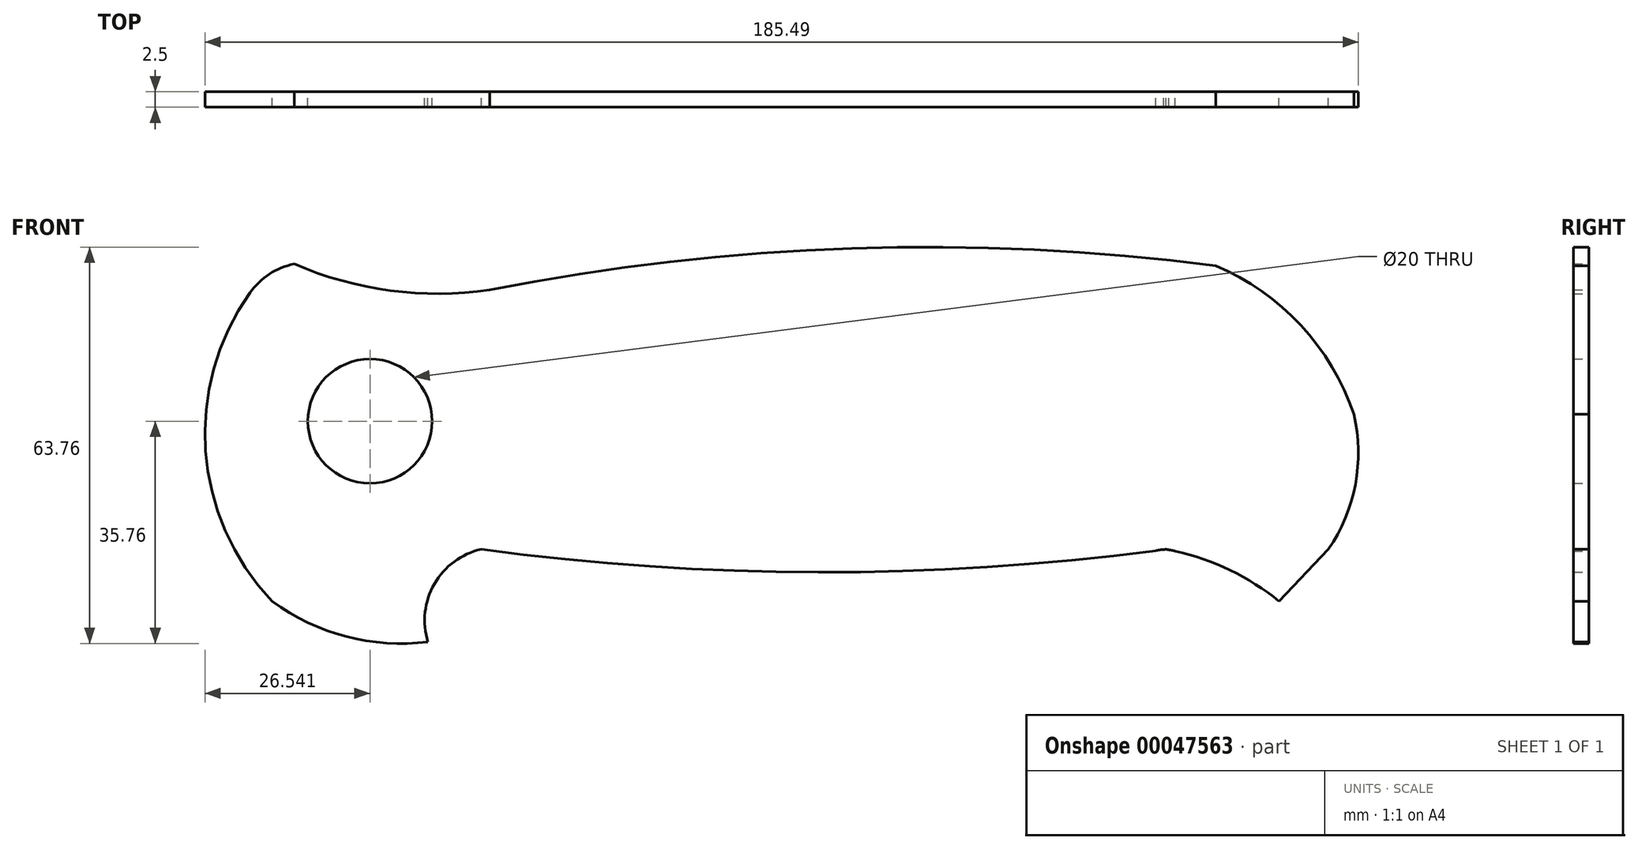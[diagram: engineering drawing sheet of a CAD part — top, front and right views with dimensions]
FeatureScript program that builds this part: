
annotation { "Feature Type Name" : "Feature", "Feature Type Description" : "" }
export const myFeature = defineFeature(function(context is Context, id is Id, definition is map)
    precondition{}
    {
        {
            var Q0;
            Q0=qCreatedBy(makeId("Front.planeOp"),FACE);
            var sketch = newSketch(context, id + "F0", { "sketchPlane" : qUnion([Q0])});
            skPoint(sketch, "E0.start.orphan", {"position": v(13.34, 2.67) * mm});
            skPoint(sketch, "E1.end.orphan", {"position": v(-22.24, -2.7) * mm});
            skPoint(sketch, "E1.start.orphan", {"position": v(-22.24, 18.65) * mm});
            skPoint(sketch, "E2.end.orphan", {"position": v(98.64, 2.67) * mm});
            skPoint(sketch, "E3.start.orphan", {"position": v(151.74, 0) * mm});
            skLineSegment(sketch, "E4.bottom", {"start": v(2.38, 0) * mm, "end": v(4.2, 0) * mm});
            skArc(sketch, "E5", {"start": v(173.95, -23.89) * mm, "mid": v(165.41, -9.56) * mm, "end": v(151.74, 0) * mm});
            skArc(sketch, "E6", {"start": v(169.86, -45.6) * mm, "mid": v(174.19, -35.18) * mm, "end": v(173.95, -23.89) * mm});
            skLineSegment(sketch, "E7", {"start": v(169.86, -45.6) * mm, "end": v(161.9, -53.97) * mm});
            skArc(sketch, "E8", {"start": v(161.9, -53.97) * mm, "mid": v(153.35, -48.62) * mm, "end": v(143.72, -45.6) * mm});
            skArc(sketch, "E9", {"start": v(33.6, -45.6) * mm, "mid": v(88.66, -49.3) * mm, "end": v(143.72, -45.6) * mm});
            skArc(sketch, "E10", {"start": v(145.2, -45.9) * mm, "mid": v(143.63, -45.65) * mm, "end": v(142.05, -45.83) * mm});
            skArc(sketch, "E11", {"start": v(-3.5, -4.21) * mm, "mid": v(-10.73, -29.72) * mm, "end": v(0, -53.97) * mm});
            skArc(sketch, "E12", {"start": v(0, -53.97) * mm, "mid": v(11.88, -59.64) * mm, "end": v(25.02, -60.49) * mm});
            skArc(sketch, "E13", {"start": v(33.6, -45.6) * mm, "mid": v(26.06, -51.17) * mm, "end": v(25.02, -60.49) * mm});
            skCircle(sketch, "E14", {"center": v(15.71, -25) * mm, "radius": 10 * mm});
            skArc(sketch, "E15", {"start": v(3.52, 0.29) * mm, "mid": v(-0.46, -1.33) * mm, "end": v(-3.57, -4.3) * mm});
            skArc(sketch, "E16", {"start": v(3.52, 0.29) * mm, "mid": v(18.96, -3.98) * mm, "end": v(34.97, -3.9) * mm});
            skArc(sketch, "E17", {"start": v(151.74, 0) * mm, "mid": v(93.2, 2.8) * mm, "end": v(34.97, -3.9) * mm});
            skSolve(sketch);
        }
        {
            var Q0;
            {var subQ0=sQuery(id+"F0.wireOp",EDGE,"E15");var subQ3=sQuery(id+"F0.wireOp",EDGE,"E4.bottom");var subQ4=makeQuery(id+"F0.imprint","INTERSECT",VERTEX,{"derivedFrom":[subQ3,subQ0]});Q0=makeQuery(id+"F0.imprint","IMPRINT",FACE,{"disambiguationData":[TD([[makeQuery(id+"F0.imprint","IMPRINT",EDGE,{"disambiguationData":[TD([[subQ4,-1.0]])],"derivedFrom":subQ3}),1.0]])]});}
            var Q1;
            {var subQ0=sQuery(id+"F0.wireOp",EDGE,"E17");var subQ1=sQuery(id+"F0.wireOp",EDGE,"E4.bottom");var subQ2=makeQuery(id+"F0.imprint","INTERSECT",VERTEX,{"derivedFrom":[subQ1,subQ0]});Q1=makeQuery(id+"F0.imprint","IMPRINT",FACE,{"disambiguationData":[TD([[makeQuery(id+"F0.imprint","IMPRINT",EDGE,{"disambiguationData":[TD([[subQ2,-1.0]])],"derivedFrom":subQ1}),1.0]])]});}
            var Q2;
            {var subQ0=sQuery(id+"F0.wireOp",EDGE,"E12");Q2=makeQuery(id+"F0.imprint","IMPRINT",FACE,{"disambiguationData":[TD([[makeQuery(id+"F0.imprint","IMPRINT",EDGE,{"derivedFrom":subQ0}),1.0]])]});}
            var Q3;
            {var subQ2=sQuery(id+"F0.wireOp",EDGE,"E4.right");Q3=makeQuery(id+"F0.imprint","IMPRINT",FACE,{"disambiguationData":[TD([[makeQuery(id+"F0.imprint","IMPRINT",EDGE,{"derivedFrom":subQ2}),1.0]])]});}
            var Q4;
            {var subQ0=sQuery(id+"F0.wireOp",EDGE,"E15");var subQ1=sQuery(id+"F0.wireOp",EDGE,"E11");var subQ3=makeQuery(id+"F0.imprint","INTERSECT",VERTEX,{"disambiguationData":[OD(0.0)],"derivedFrom":[subQ1,subQ0]});Q4=makeQuery(id+"F0.imprint","IMPRINT",FACE,{"disambiguationData":[TD([[makeQuery(id+"F0.imprint","IMPRINT",EDGE,{"disambiguationData":[TD([[subQ3,-1.0]])],"derivedFrom":subQ1}),-1.0]])]});}
            var Q5;
            {var subQ5=sQuery(id+"F0.wireOp",EDGE,"E10");var subQ8=sQuery(id+"F0.wireOp",EDGE,"E8");var subQ10=makeQuery(id+"F0.imprint","INTERSECT",VERTEX,{"disambiguationData":[OD(0.0)],"derivedFrom":[subQ8,subQ5]});Q5=makeQuery(id+"F0.imprint","IMPRINT",FACE,{"disambiguationData":[TD([[makeQuery(id+"F0.imprint","IMPRINT",EDGE,{"disambiguationData":[TD([[subQ10,-1.0]])],"derivedFrom":subQ8}),1.0]])]});}
            var Q6;
            {var subQ18=sQuery(id+"F0.wireOp",EDGE,"E4.right");Q6=makeQuery(id+"F0.imprint","IMPRINT",FACE,{"disambiguationData":[TD([[makeQuery(id+"F0.imprint","IMPRINT",EDGE,{"derivedFrom":subQ18}),-1.0]])]});}
            extrude(context, id + "F1", {"entities" : qUnion([Q0, Q1, Q2, Q3, Q4, Q5, Q6]), "depth" : 2.5 * mm});
        }
    });
